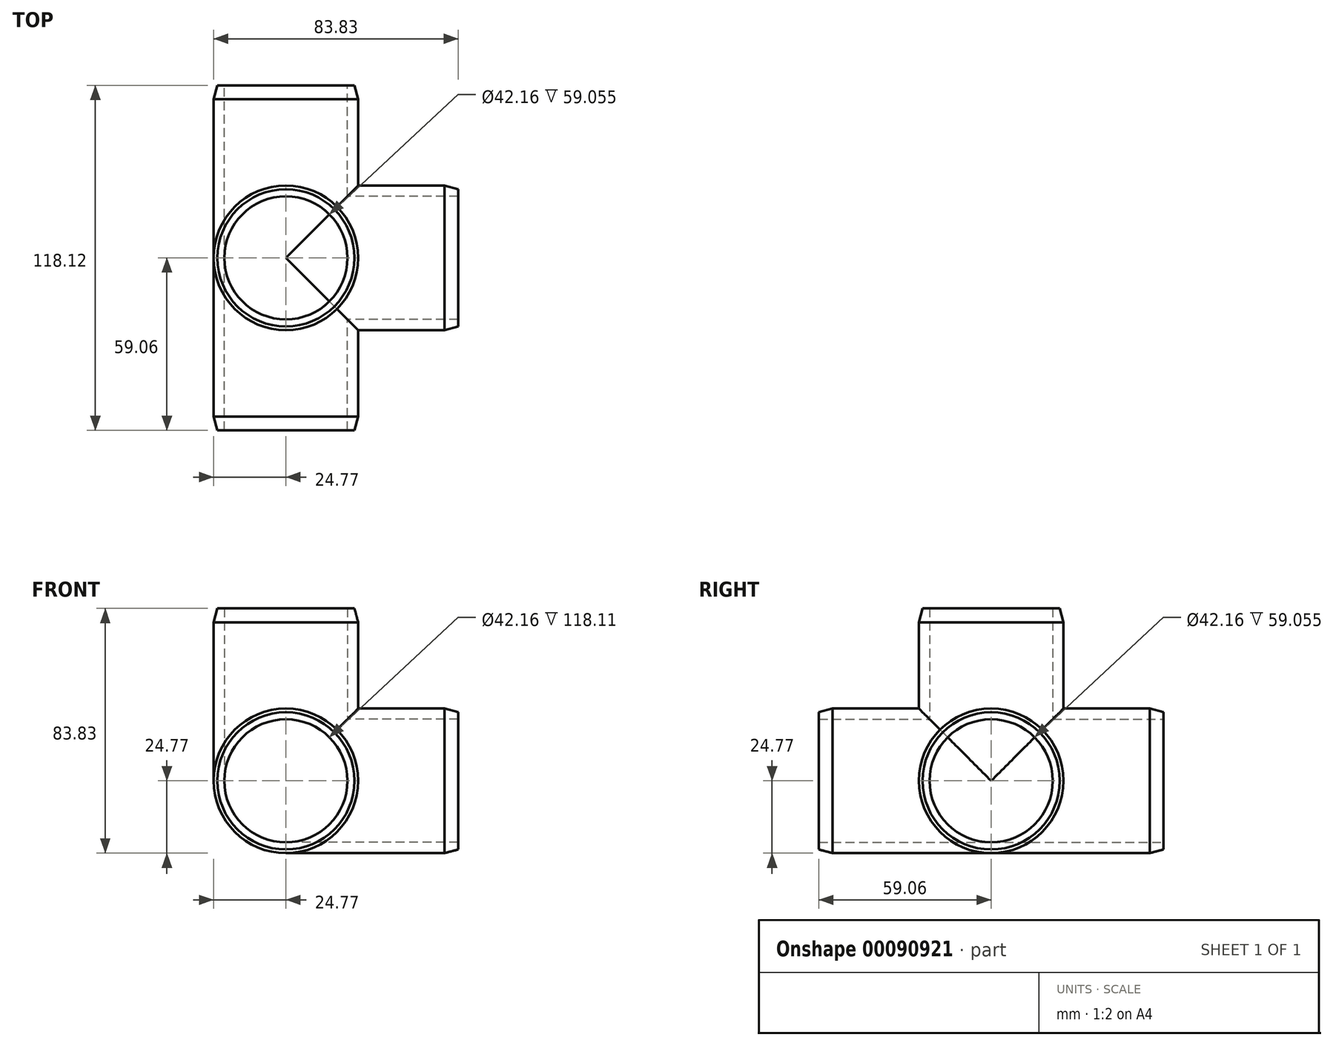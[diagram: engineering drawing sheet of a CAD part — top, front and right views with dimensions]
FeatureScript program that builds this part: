
annotation { "Feature Type Name" : "Feature", "Feature Type Description" : "" }
export const myFeature = defineFeature(function(context is Context, id is Id, definition is map)
    precondition{}
    {
        {
            var Q0;
            Q0=qCreatedBy(makeId("Front.planeOp"),FACE);
            var sketch = newSketch(context, id + "F0", { "sketchPlane" : qUnion([Q0])});
            skCircle(sketch, "E0", {"center": v(0, 0) * mm, "radius": 21.08 * mm});
            skCircle(sketch, "E1.0", {"center": v(0, 0) * mm, "radius": 24.77 * mm});
            skSolve(sketch);
        }
        {
            var Q0;
            Q0=qSketchRegion(id+"F0",true);
            extrude(context, id + "F1", {"entities" : qUnion([Q0]), "endBound" : BoundingType.SYMMETRIC, "depth" : 118.11 * mm});
        }
        {
            var Q0;
            Q0=qCreatedBy(makeId("Top.planeOp"),FACE);
            var sketch = newSketch(context, id + "F2", { "sketchPlane" : qUnion([Q0])});
            skCircle(sketch, "E2", {"center": v(0, 0) * mm, "radius": 21.08 * mm});
            skCircle(sketch, "E3.0", {"center": v(0, 0) * mm, "radius": 24.77 * mm});
            skSolve(sketch);
        }
        {
            var Q0;
            Q0=qSketchRegion(id+"F2",true);
            extrude(context, id + "F3", {"entities" : qUnion([Q0]), "operationType" : NewBodyOperationType.ADD, "depth" : 59.05 * mm});
        }
        {
            var Q0;
            Q0=qCreatedBy(makeId("Right.planeOp"),FACE);
            var sketch = newSketch(context, id + "F4", { "sketchPlane" : qUnion([Q0])});
            skCircle(sketch, "E4", {"center": v(0, 0) * mm, "radius": 21.08 * mm});
            skCircle(sketch, "E5.0", {"center": v(0, 0) * mm, "radius": 24.77 * mm});
            skSolve(sketch);
        }
        {
            var Q0;
            Q0=qSketchRegion(id+"F4",true);
            extrude(context, id + "F5", {"entities" : qUnion([Q0]), "operationType" : NewBodyOperationType.ADD, "depth" : 59.05 * mm});
        }
        {
            var Q0;
            Q0=makeQuery(id+"F4.imprint","IMPRINT",FACE,{"disambiguationData":[TD([[makeQuery(id+"F4.imprint","IMPRINT",EDGE,{"derivedFrom":sQuery(id+"F4.wireOp",EDGE,"E4")}),1.0]])]});
            extrude(context, id + "F6", {"entities" : qUnion([Q0]), "operationType" : NewBodyOperationType.REMOVE, "endBound" : BoundingType.THROUGH_ALL, "depth" : 25.4 * mm});
        }
        {
            var Q0;
            Q0=makeQuery(id+"F2.imprint","IMPRINT",FACE,{"disambiguationData":[TD([[makeQuery(id+"F2.imprint","IMPRINT",EDGE,{"derivedFrom":sQuery(id+"F2.wireOp",EDGE,"E2")}),1.0]])]});
            extrude(context, id + "F7", {"entities" : qUnion([Q0]), "operationType" : NewBodyOperationType.REMOVE, "endBound" : BoundingType.THROUGH_ALL, "depth" : 25.4 * mm});
        }
        {
            var Q0;
            Q0=makeQuery(id+"F0.imprint","IMPRINT",FACE,{"disambiguationData":[TD([[makeQuery(id+"F0.imprint","IMPRINT",EDGE,{"derivedFrom":sQuery(id+"F0.wireOp",EDGE,"E0")}),1.0]])]});
            extrude(context, id + "F8", {"entities" : qUnion([Q0]), "operationType" : NewBodyOperationType.REMOVE, "endBound" : BoundingType.THROUGH_ALL, "depth" : 25.4 * mm, "hasSecondDirection" : true, "secondDirectionBound" : SecondDirectionBoundingType.THROUGH_ALL, "secondDirectionOppositeDirection" : true, "secondDirectionDepth" : 25.4 * mm});
        }
        {
            var Q0;
            Q0=makeQuery(id+"F3.opExtrude","CAP_EDGE",EDGE,{"disambiguationData":[OSD([sQuery(id+"F2.wireOp",EDGE,"E3.0")])],"isStart":false});
            var Q1;
            Q1=makeQuery(id+"F1.opExtrude","CAP_EDGE",EDGE,{"disambiguationData":[OSD([sQuery(id+"F0.wireOp",EDGE,"E1.0")])],"isStart":false});
            var Q2;
            Q2=makeQuery(id+"F5.opExtrude","CAP_EDGE",EDGE,{"disambiguationData":[OSD([sQuery(id+"F4.wireOp",EDGE,"E5.0")])],"isStart":false});
            chamfer(context, id + "F9", {"entities" : qUnion([Q0, Q1, Q2]), "chamferType" : ChamferType.OFFSET_ANGLE, "width" : 1.27 * mm, "oppositeDirection" : false, "angle" : 75 * degree, "tangentPropagation" : true});
        }
        {
            var Q0;
            Q0=makeQuery(id+"F1.opExtrude","CAP_EDGE",EDGE,{"disambiguationData":[OSD([sQuery(id+"F0.wireOp",EDGE,"E1.0")])],"isStart":true});
            chamfer(context, id + "F10", {"entities" : qUnion([Q0]), "chamferType" : ChamferType.OFFSET_ANGLE, "width" : 1.27 * mm, "oppositeDirection" : true, "angle" : 75 * degree, "tangentPropagation" : true});
        }
    });
